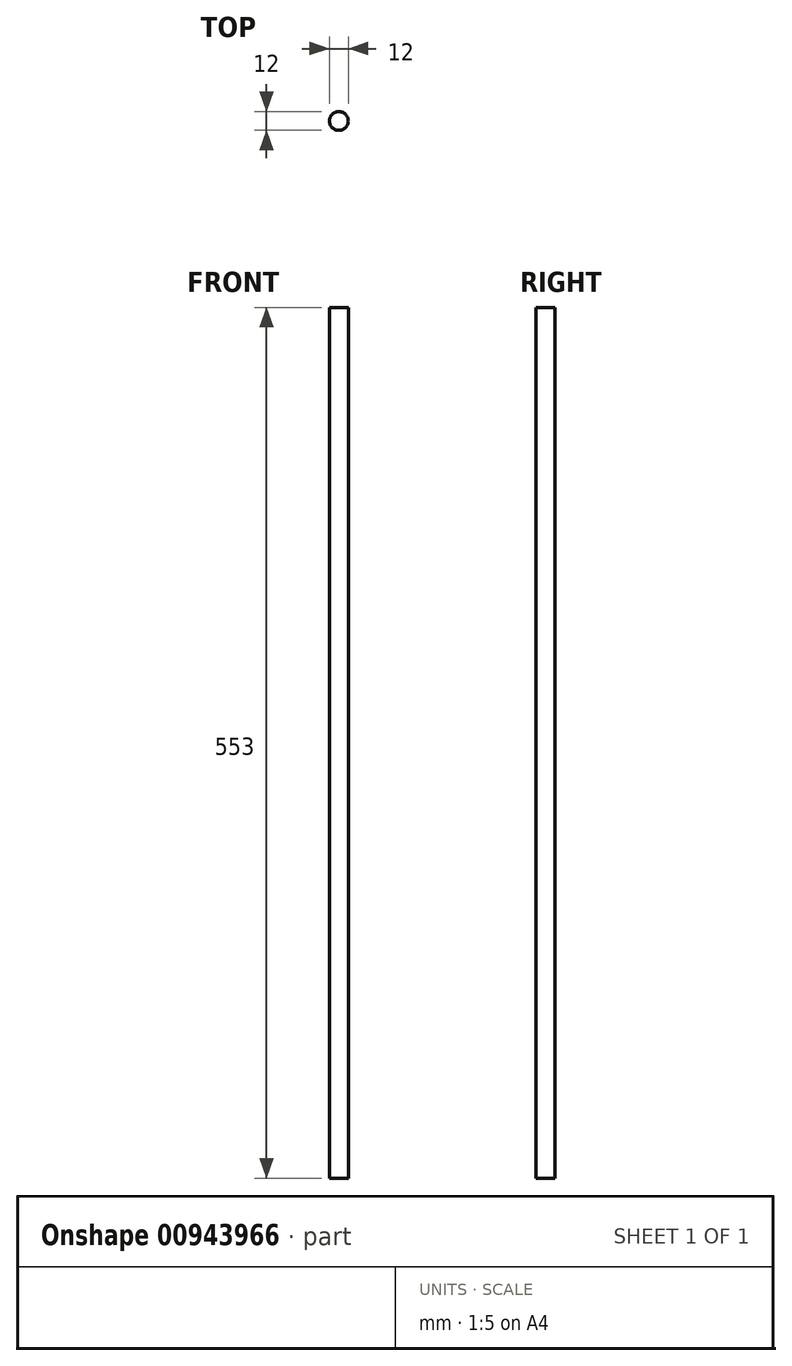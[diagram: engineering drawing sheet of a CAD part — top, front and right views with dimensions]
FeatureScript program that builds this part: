
annotation { "Feature Type Name" : "Feature", "Feature Type Description" : "" }
export const myFeature = defineFeature(function(context is Context, id is Id, definition is map)
    precondition{}
    {
        {
            var Q0;
            Q0=qCreatedBy(makeId("Top.planeOp"),FACE);
            var sketch = newSketch(context, id + "F0", { "sketchPlane" : qUnion([Q0])});
            skCircle(sketch, "E0", {"center": v(0, 0) * mm, "radius": 6 * mm});
            skSolve(sketch);
        }
        {
            var Q0;
            Q0=makeQuery(id+"F0.imprint","IMPRINT",FACE,{"disambiguationData":[TD([[makeQuery(id+"F0.imprint","IMPRINT",EDGE,{"derivedFrom":sQuery(id+"F0.wireOp",EDGE,"E0")}),1.0]])]});
            extrude(context, id + "F1", {"entities" : qUnion([Q0]), "depth" : 553 * mm, "offsetDistance" : 25 * mm});
        }
    });
